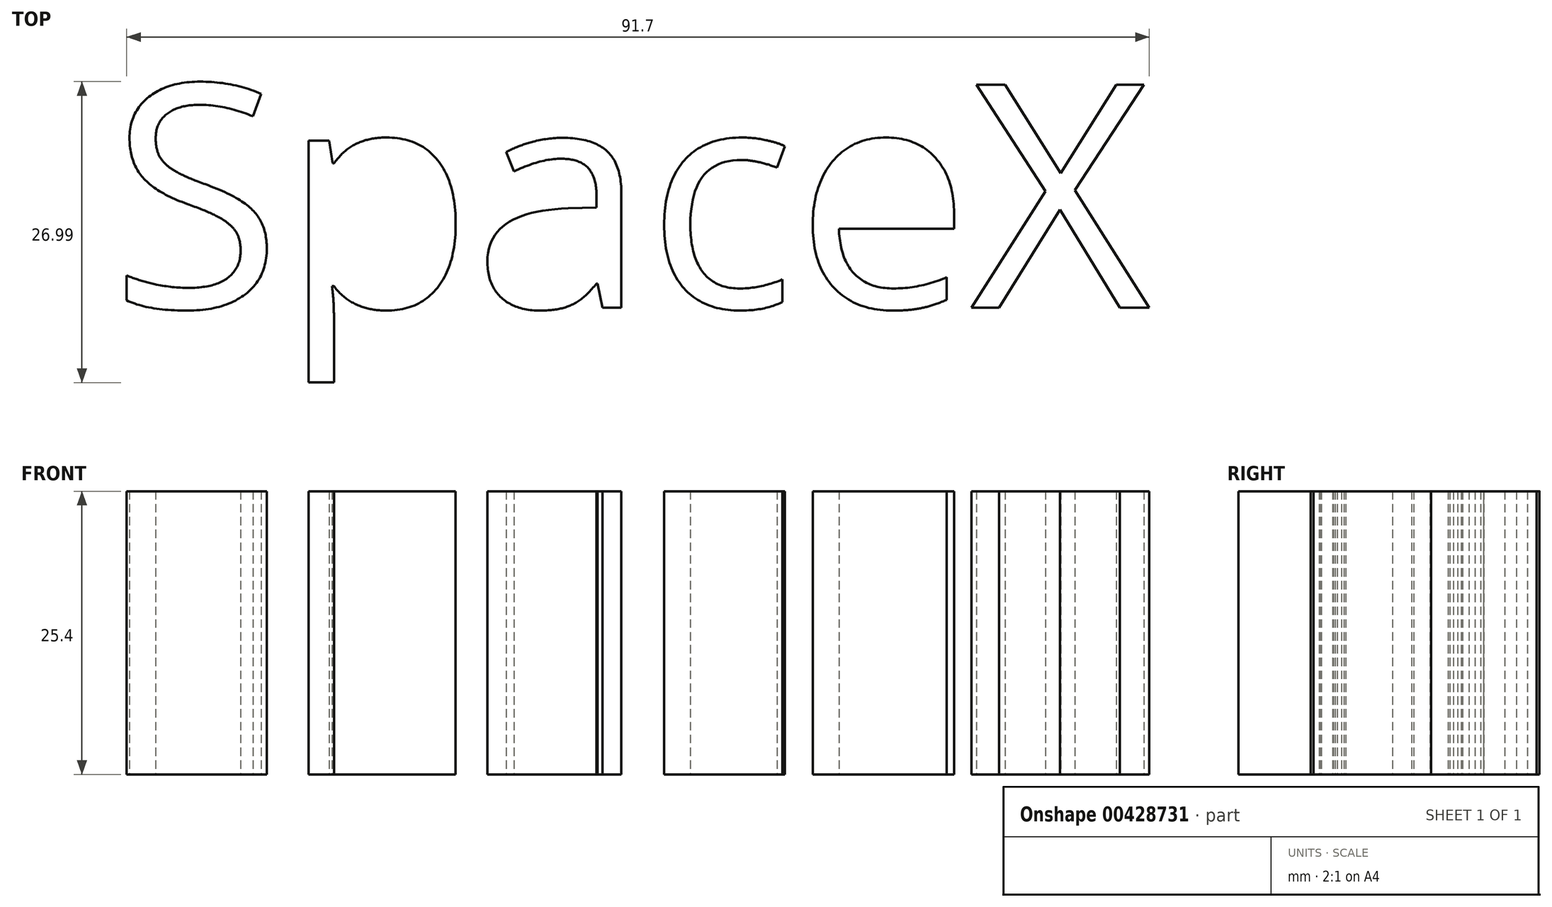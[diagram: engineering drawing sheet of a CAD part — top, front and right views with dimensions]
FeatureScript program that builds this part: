
annotation { "Feature Type Name" : "Feature", "Feature Type Description" : "" }
export const myFeature = defineFeature(function(context is Context, id is Id, definition is map)
    precondition{}
    {
        {
            var Q0;
            Q0=qCreatedBy(makeId("Top.planeOp"),FACE);
            var sketch = newSketch(context, id + "F0", { "sketchPlane" : qUnion([Q0])});
            skText(sketch, "E0", { "text": "SpaceX", "fontName": "OpenSans-Regular.ttf"});
            const initialGuessF0  = {"E0": [-0.06158, 0.03284, 1, 0, 0.02015]};
            skSetInitialGuess(sketch, initialGuessF0);
            skSolve(sketch);
        }
        {
            var Q0;
            Q0=makeQuery(id+"F0.imprint","IMPRINT",FACE,{"disambiguationData":[TD([[makeQuery(id+"F0.imprint","IMPRINT",EDGE,{"derivedFrom":sQuery(id+"F0.wireOp",EDGE,"E0.sketch_text.stroke-0")}),-1.0]])]});
            var Q1;
            Q1=makeQuery(id+"F0.imprint","IMPRINT",FACE,{"disambiguationData":[TD([[makeQuery(id+"F0.imprint","IMPRINT",EDGE,{"derivedFrom":sQuery(id+"F0.wireOp",EDGE,"E0.sketch_text.stroke-77")}),-1.0]])]});
            var Q2;
            Q2=makeQuery(id+"F0.imprint","IMPRINT",FACE,{"disambiguationData":[TD([[makeQuery(id+"F0.imprint","IMPRINT",EDGE,{"derivedFrom":sQuery(id+"F0.wireOp",EDGE,"E0.sketch_text.stroke-111")}),-1.0]])]});
            var Q3;
            Q3=makeQuery(id+"F0.imprint","IMPRINT",FACE,{"disambiguationData":[TD([[makeQuery(id+"F0.imprint","IMPRINT",EDGE,{"derivedFrom":sQuery(id+"F0.wireOp",EDGE,"E0.sketch_text.stroke-25")}),-1.0]])]});
            var Q4;
            Q4=makeQuery(id+"F0.imprint","IMPRINT",FACE,{"disambiguationData":[TD([[makeQuery(id+"F0.imprint","IMPRINT",EDGE,{"derivedFrom":sQuery(id+"F0.wireOp",EDGE,"E0.sketch_text.stroke-41")}),1.0]])]});
            var Q5;
            Q5=makeQuery(id+"F0.imprint","IMPRINT",FACE,{"disambiguationData":[TD([[makeQuery(id+"F0.imprint","IMPRINT",EDGE,{"derivedFrom":sQuery(id+"F0.wireOp",EDGE,"E0.sketch_text.stroke-50")}),-1.0]])]});
            var Q6;
            Q6=makeQuery(id+"F0.imprint","IMPRINT",FACE,{"disambiguationData":[TD([[makeQuery(id+"F0.imprint","IMPRINT",EDGE,{"derivedFrom":sQuery(id+"F0.wireOp",EDGE,"E0.sketch_text.stroke-69")}),1.0]])]});
            var Q7;
            Q7=makeQuery(id+"F0.imprint","IMPRINT",FACE,{"disambiguationData":[TD([[makeQuery(id+"F0.imprint","IMPRINT",EDGE,{"derivedFrom":sQuery(id+"F0.wireOp",EDGE,"E0.sketch_text.stroke-92")}),-1.0]])]});
            var Q8;
            Q8=makeQuery(id+"F0.imprint","IMPRINT",FACE,{"disambiguationData":[TD([[makeQuery(id+"F0.imprint","IMPRINT",EDGE,{"derivedFrom":sQuery(id+"F0.wireOp",EDGE,"E0.sketch_text.stroke-106")}),1.0]])]});
            extrude(context, id + "F1", {"entities" : qUnion([Q0, Q1, Q2, Q3, Q4, Q5, Q6, Q7, Q8]), "depth" : 25.4 * mm});
        }
    });
